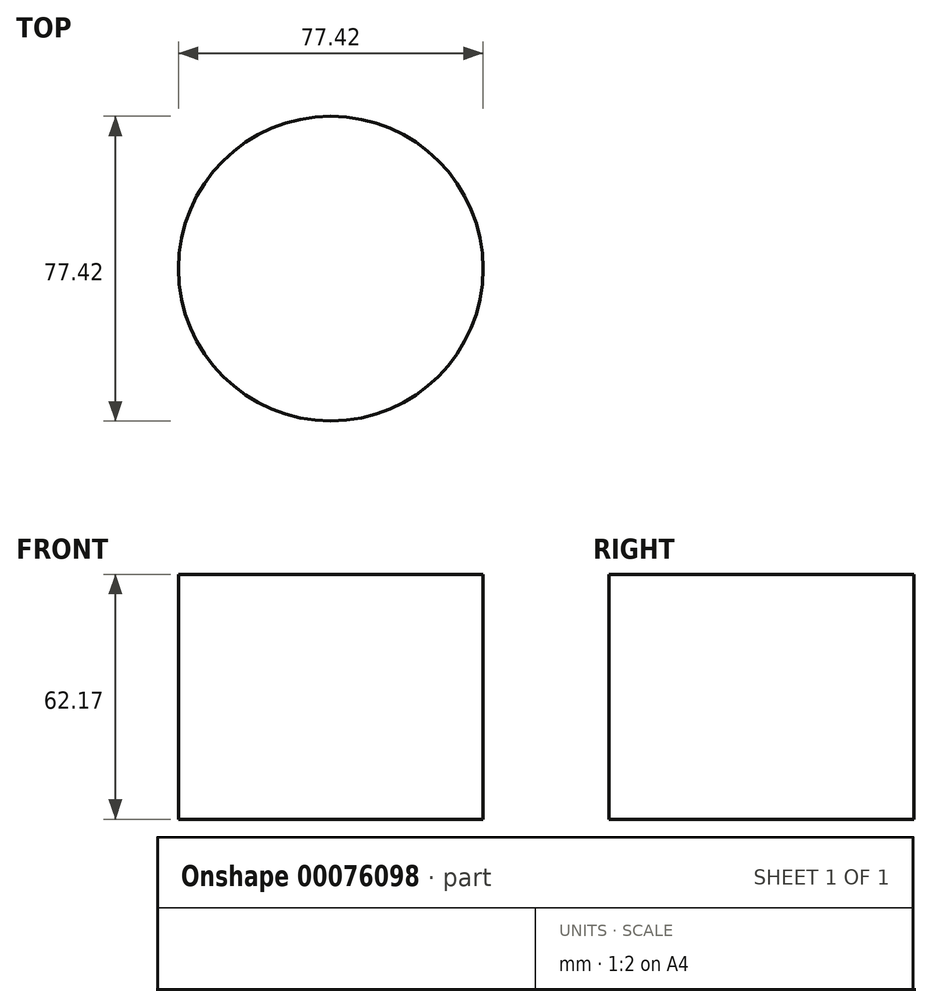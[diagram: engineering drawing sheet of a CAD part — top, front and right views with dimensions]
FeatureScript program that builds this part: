
annotation { "Feature Type Name" : "Feature", "Feature Type Description" : "" }
export const myFeature = defineFeature(function(context is Context, id is Id, definition is map)
    precondition{}
    {
        {
            var Q0;
            Q0=qCreatedBy(makeId("Top.planeOp"),FACE);
            var sketch = newSketch(context, id + "F0", { "sketchPlane" : qUnion([Q0])});
            skCircle(sketch, "E0", {"center": v(0, 0) * mm, "radius": 38.71 * mm});
            skSolve(sketch);
        }
        {
            var Q0;
            Q0 = qSketchRegion(id + "F0", true);
            extrude(context, id + "F1", {"entities" : qUnion([Q0]), "depth" : 62.17 * mm});
        }
    });
